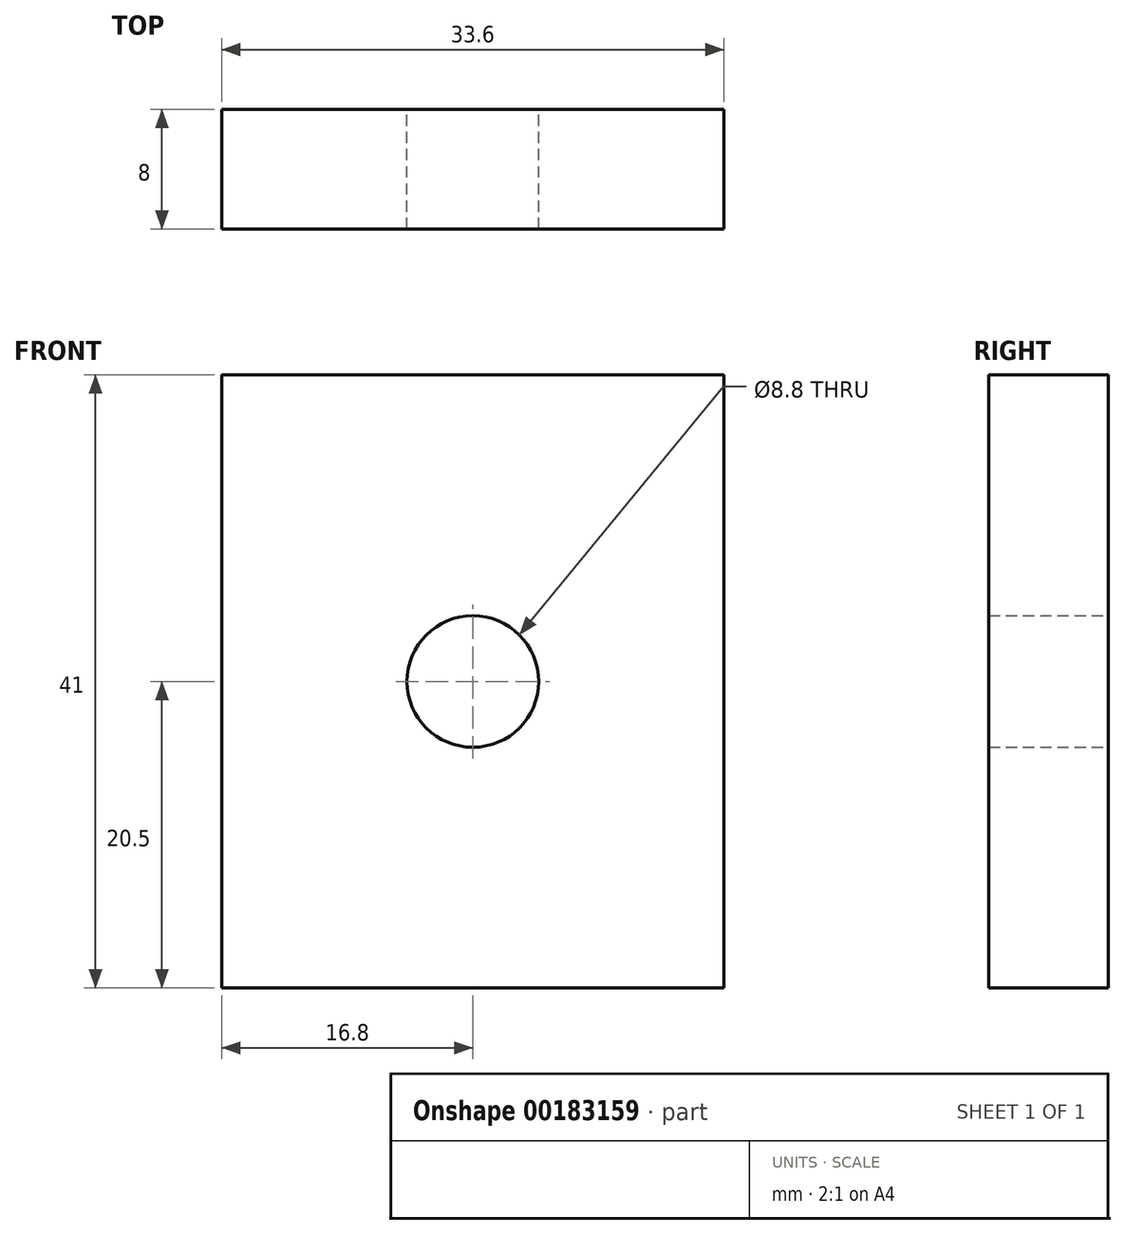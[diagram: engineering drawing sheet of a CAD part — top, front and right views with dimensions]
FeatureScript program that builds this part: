
annotation { "Feature Type Name" : "Feature", "Feature Type Description" : "" }
export const myFeature = defineFeature(function(context is Context, id is Id, definition is map)
    precondition{}
    {
        {
            var Q0;
            Q0=qCreatedBy(makeId("Top.planeOp"),FACE);
            var sketch = newSketch(context, id + "F0", { "sketchPlane" : qUnion([Q0])});
            skLineSegment(sketch, "E0.bottom", {"start": v(0, 0) * mm, "end": v(33.6, 0) * mm});
            skLineSegment(sketch, "E0.top", {"start": v(0, 8) * mm, "end": v(33.6, 8) * mm});
            skLineSegment(sketch, "E0.left", {"start": v(0, 0) * mm, "end": v(0, 8) * mm});
            skLineSegment(sketch, "E0.right", {"start": v(33.6, 0) * mm, "end": v(33.6, 8) * mm});
            skSolve(sketch);
        }
        {
            var Q0;
            Q0 = qSketchRegion(id + "F0", true);
            extrude(context, id + "F1", {"entities" : qUnion([Q0]), "depth" : 41 * mm});
        }
        {
            var Q0;
            Q0=makeQuery(id+"F1.opExtrude","SWEPT_FACE",FACE,{"disambiguationData":[OSD([sQuery(id+"F0.wireOp",EDGE,"E0.top")])]});
            var sketch = newSketch(context, id + "F2", { "sketchPlane" : qUnion([Q0])});
            skCircle(sketch, "E1", {"center": v(-16.8, 20.5) * mm, "radius": 3.08 * mm});
            skPoint(sketch, "E1.centerSnap0", {"position": v(-16.8, 0) * mm});
            skPoint(sketch, "E1.centerSnap1", {"position": v(-33.6, 20.5) * mm});
            skSolve(sketch);
        }
        {
            var Q0;
            Q0=sQuery(id+"F2.wireOp",VERTEX,"E1.center");
            var Q1;
            Q1=makeQuery(id+"F1.opExtrude","SWEPT_BODY",BODY,{"disambiguationData":[OSD([sQuery(id+"F0.wireOp",EDGE,"E0.bottom"),sQuery(id+"F0.wireOp",EDGE,"E0.top"),sQuery(id+"F0.wireOp",EDGE,"E0.left"),sQuery(id+"F0.wireOp",EDGE,"E0.right")])]});
            hole(context, id + "F3", {"style" : HoleStyle.SIMPLE, "endStyle" : HoleEndStyle.THROUGH, "standardTappedOrClearance" : lookupTablePath({ "standard" : "ISO", "engagement" : "75%", "pitch" : "1.25 mm", "size" : "M10", "type" : "Tapped" }), "standardBlindInLast" : lookupTablePath({ "standard" : "ISO", "engagement" : "75%", "pitch" : "1.25 mm", "size" : "M10", "type" : "Tapped" }), "holeDiameter" : 8.8 * mm, "locations" : qUnion([Q0]), "scope" : qUnion([Q1]), "isTappedThrough" : true, "majorDiameter" : 10 * mm, "showTappedDepth" : true});
        }
    });
